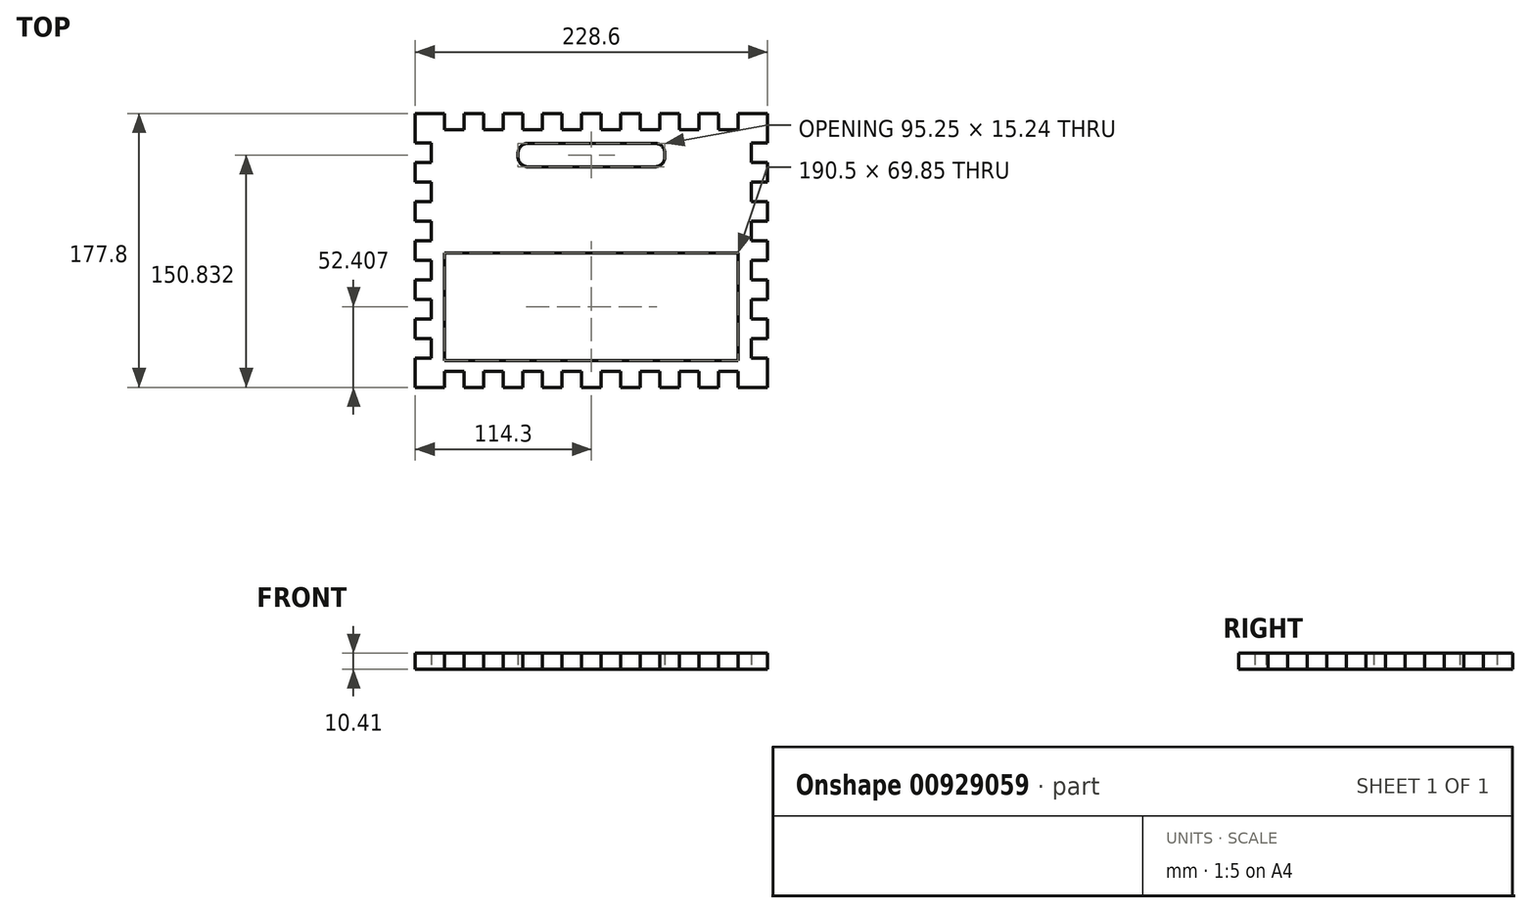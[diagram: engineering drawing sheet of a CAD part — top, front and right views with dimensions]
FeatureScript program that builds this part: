
annotation { "Feature Type Name" : "Feature", "Feature Type Description" : "" }
export const myFeature = defineFeature(function(context is Context, id is Id, definition is map)
    precondition{}
    {
        {
            var Q0;
            Q0=qCreatedBy(makeId("Top.planeOp"),FACE);
            var sketch = newSketch(context, id + "F0", { "sketchPlane" : qUnion([Q0])});
            skLineSegment(sketch, "E0.bottom", {"start": v(0, 0) * mm, "end": v(19.05, 0) * mm});
            skLineSegment(sketch, "E0.left", {"start": v(0, 0) * mm, "end": v(0, -19.05) * mm});
            skLineSegment(sketch, "E1", {"start": v(19.05, 0) * mm, "end": v(19.05, -10.41) * mm});
            skLineSegment(sketch, "E2", {"start": v(19.05, -10.41) * mm, "end": v(31.75, -10.41) * mm});
            skLineSegment(sketch, "E3", {"start": v(31.75, -10.41) * mm, "end": v(31.75, 0) * mm});
            skLineSegment(sketch, "E4", {"start": v(31.75, 0) * mm, "end": v(44.45, 0) * mm});
            skLineSegment(sketch, "E5", {"start": v(44.45, 0) * mm, "end": v(44.45, -10.41) * mm});
            skLineSegment(sketch, "E6", {"start": v(44.45, -10.41) * mm, "end": v(57.15, -10.41) * mm});
            skLineSegment(sketch, "E7", {"start": v(57.15, -10.41) * mm, "end": v(57.15, 0) * mm});
            skLineSegment(sketch, "E8", {"start": v(57.15, 0) * mm, "end": v(69.85, 0) * mm});
            skLineSegment(sketch, "E9", {"start": v(69.85, 0) * mm, "end": v(69.85, -10.41) * mm});
            skLineSegment(sketch, "E10", {"start": v(69.85, -10.41) * mm, "end": v(82.55, -10.41) * mm});
            skLineSegment(sketch, "E11", {"start": v(82.55, -10.41) * mm, "end": v(82.55, 0) * mm});
            skLineSegment(sketch, "E12.trimOffspring", {"start": v(82.55, 0) * mm, "end": v(95.25, 0) * mm});
            skLineSegment(sketch, "E13", {"start": v(95.25, 0) * mm, "end": v(95.25, -10.41) * mm});
            skLineSegment(sketch, "E14", {"start": v(95.25, -10.41) * mm, "end": v(107.95, -10.41) * mm});
            skLineSegment(sketch, "E15", {"start": v(107.95, -10.41) * mm, "end": v(107.95, 0) * mm});
            skLineSegment(sketch, "E16", {"start": v(107.95, 0) * mm, "end": v(120.65, 0) * mm});
            skLineSegment(sketch, "E17", {"start": v(120.65, 0) * mm, "end": v(120.65, -10.41) * mm});
            skLineSegment(sketch, "E18", {"start": v(120.65, -10.41) * mm, "end": v(133.35, -10.41) * mm});
            skLineSegment(sketch, "E19", {"start": v(133.35, -10.41) * mm, "end": v(133.35, 0) * mm});
            skLineSegment(sketch, "E20", {"start": v(133.35, 0) * mm, "end": v(146.05, 0) * mm});
            skLineSegment(sketch, "E21", {"start": v(146.05, 0) * mm, "end": v(146.05, -10.41) * mm});
            skLineSegment(sketch, "E22", {"start": v(146.05, -10.41) * mm, "end": v(158.75, -10.41) * mm});
            skLineSegment(sketch, "E23", {"start": v(158.75, -10.41) * mm, "end": v(158.75, 0) * mm});
            skLineSegment(sketch, "E24.trimOffspring", {"start": v(158.75, 0) * mm, "end": v(171.45, 0) * mm});
            skLineSegment(sketch, "E25", {"start": v(171.45, 0) * mm, "end": v(171.45, -10.41) * mm});
            skLineSegment(sketch, "E26", {"start": v(171.45, -10.41) * mm, "end": v(184.15, -10.41) * mm});
            skLineSegment(sketch, "E27", {"start": v(184.15, -10.41) * mm, "end": v(184.15, 0) * mm});
            skLineSegment(sketch, "E28", {"start": v(184.15, 0) * mm, "end": v(196.85, 0) * mm});
            skLineSegment(sketch, "E29", {"start": v(196.85, 0) * mm, "end": v(196.85, -10.41) * mm});
            skLineSegment(sketch, "E30", {"start": v(196.85, -10.41) * mm, "end": v(209.55, -10.41) * mm});
            skLineSegment(sketch, "E31", {"start": v(209.55, -10.41) * mm, "end": v(209.55, 0) * mm});
            skLineSegment(sketch, "E32.trimOffspring", {"start": v(209.55, 0) * mm, "end": v(228.6, 0) * mm});
            skLineSegment(sketch, "E33", {"start": v(0, -19.05) * mm, "end": v(10.41, -19.05) * mm});
            skLineSegment(sketch, "E34", {"start": v(10.41, -19.05) * mm, "end": v(10.41, -31.75) * mm});
            skLineSegment(sketch, "E35", {"start": v(10.41, -31.75) * mm, "end": v(0, -31.75) * mm});
            skLineSegment(sketch, "E36", {"start": v(0, -31.75) * mm, "end": v(0, -44.45) * mm});
            skLineSegment(sketch, "E37", {"start": v(0, -44.45) * mm, "end": v(10.41, -44.45) * mm});
            skLineSegment(sketch, "E38", {"start": v(10.41, -44.45) * mm, "end": v(10.41, -57.15) * mm});
            skLineSegment(sketch, "E39", {"start": v(10.41, -57.15) * mm, "end": v(0, -57.15) * mm});
            skLineSegment(sketch, "E40", {"start": v(0, -57.15) * mm, "end": v(0, -69.85) * mm});
            skLineSegment(sketch, "E41", {"start": v(0, -69.85) * mm, "end": v(10.41, -69.85) * mm});
            skLineSegment(sketch, "E42", {"start": v(10.41, -69.85) * mm, "end": v(10.41, -82.55) * mm});
            skLineSegment(sketch, "E43", {"start": v(10.41, -82.55) * mm, "end": v(0, -82.55) * mm});
            skLineSegment(sketch, "E44.trimOffspring", {"start": v(0, -82.55) * mm, "end": v(0, -95.25) * mm});
            skLineSegment(sketch, "E45", {"start": v(0, -95.25) * mm, "end": v(10.41, -95.25) * mm});
            skLineSegment(sketch, "E46", {"start": v(10.41, -95.25) * mm, "end": v(10.41, -107.95) * mm});
            skLineSegment(sketch, "E47", {"start": v(10.41, -107.95) * mm, "end": v(0, -107.95) * mm});
            skLineSegment(sketch, "E48", {"start": v(0, -107.95) * mm, "end": v(0, -120.65) * mm});
            skLineSegment(sketch, "E49", {"start": v(0, -120.65) * mm, "end": v(10.41, -120.65) * mm});
            skLineSegment(sketch, "E50", {"start": v(10.41, -120.65) * mm, "end": v(10.41, -133.35) * mm});
            skLineSegment(sketch, "E51", {"start": v(10.41, -133.35) * mm, "end": v(0, -133.35) * mm});
            skLineSegment(sketch, "E52", {"start": v(0, -133.35) * mm, "end": v(0, -146.05) * mm});
            skLineSegment(sketch, "E53", {"start": v(0, -146.05) * mm, "end": v(10.41, -146.05) * mm});
            skLineSegment(sketch, "E54", {"start": v(10.41, -146.05) * mm, "end": v(10.41, -158.75) * mm});
            skLineSegment(sketch, "E55", {"start": v(10.41, -158.75) * mm, "end": v(0, -158.75) * mm});
            skLineSegment(sketch, "E56.trimOffspring", {"start": v(0, -158.75) * mm, "end": v(0, -177.8) * mm});
            skLineSegment(sketch, "E57", {"start": v(114.3, 0) * mm, "end": v(114.3, 0) * mm});
            skLineSegment(sketch, "E58", {"start": v(0, -88.9) * mm, "end": v(0, -88.9) * mm});
            skLineSegment(sketch, "E59.MirrorCS", {"start": v(218.19, -82.55) * mm, "end": v(228.6, -82.55) * mm});
            skLineSegment(sketch, "E60.MirrorCS", {"start": v(228.6, -69.85) * mm, "end": v(218.19, -69.85) * mm});
            skLineSegment(sketch, "E61.MirrorCS", {"start": v(228.6, -120.65) * mm, "end": v(218.19, -120.65) * mm});
            skLineSegment(sketch, "E62.MirrorCS", {"start": v(218.19, -57.15) * mm, "end": v(228.6, -57.15) * mm});
            skLineSegment(sketch, "E63.MirrorCS", {"start": v(228.6, -95.25) * mm, "end": v(218.19, -95.25) * mm});
            skLineSegment(sketch, "E64.MirrorCS", {"start": v(218.19, -158.75) * mm, "end": v(228.6, -158.75) * mm});
            skLineSegment(sketch, "E65.MirrorCS", {"start": v(218.19, -107.95) * mm, "end": v(228.6, -107.95) * mm});
            skLineSegment(sketch, "E66.MirrorCS", {"start": v(228.6, -19.05) * mm, "end": v(218.19, -19.05) * mm});
            skLineSegment(sketch, "E67.MirrorCS", {"start": v(228.6, -44.45) * mm, "end": v(218.19, -44.45) * mm});
            skLineSegment(sketch, "E68.MirrorCS", {"start": v(218.19, -133.35) * mm, "end": v(228.6, -133.35) * mm});
            skLineSegment(sketch, "E69.MirrorCS", {"start": v(228.6, -82.55) * mm, "end": v(228.6, -95.25) * mm});
            skLineSegment(sketch, "E70.MirrorCS", {"start": v(218.19, -31.75) * mm, "end": v(228.6, -31.75) * mm});
            skLineSegment(sketch, "E71.MirrorCS", {"start": v(228.6, -146.05) * mm, "end": v(218.19, -146.05) * mm});
            skLineSegment(sketch, "E72.MirrorCS", {"start": v(228.6, 0) * mm, "end": v(228.6, -19.05) * mm});
            skLineSegment(sketch, "E73.MirrorCS", {"start": v(228.6, -133.35) * mm, "end": v(228.6, -146.05) * mm});
            skLineSegment(sketch, "E74.MirrorCS", {"start": v(228.6, -107.95) * mm, "end": v(228.6, -120.65) * mm});
            skLineSegment(sketch, "E75.MirrorCS", {"start": v(228.6, -31.75) * mm, "end": v(228.6, -44.45) * mm});
            skLineSegment(sketch, "E76.MirrorCS", {"start": v(228.6, -57.15) * mm, "end": v(228.6, -69.85) * mm});
            skLineSegment(sketch, "E77.MirrorCS", {"start": v(218.19, -19.05) * mm, "end": v(218.19, -31.75) * mm});
            skLineSegment(sketch, "E78.MirrorCS", {"start": v(218.19, -120.65) * mm, "end": v(218.19, -133.35) * mm});
            skLineSegment(sketch, "E79.MirrorCS", {"start": v(218.19, -69.85) * mm, "end": v(218.19, -82.55) * mm});
            skLineSegment(sketch, "E80.MirrorCS", {"start": v(218.19, -44.45) * mm, "end": v(218.19, -57.15) * mm});
            skLineSegment(sketch, "E81.MirrorCS", {"start": v(218.19, -146.05) * mm, "end": v(218.19, -158.75) * mm});
            skLineSegment(sketch, "E82.MirrorCS", {"start": v(218.19, -95.25) * mm, "end": v(218.19, -107.95) * mm});
            skLineSegment(sketch, "E83.MirrorCS", {"start": v(228.6, -158.75) * mm, "end": v(228.6, -177.8) * mm});
            skLineSegment(sketch, "E84.MirrorCS", {"start": v(69.85, -177.8) * mm, "end": v(69.85, -167.39) * mm});
            skLineSegment(sketch, "E85.MirrorCS", {"start": v(209.55, -167.39) * mm, "end": v(209.55, -177.8) * mm});
            skLineSegment(sketch, "E86.MirrorCS", {"start": v(19.05, -177.8) * mm, "end": v(19.05, -167.39) * mm});
            skLineSegment(sketch, "E87.MirrorCS", {"start": v(107.95, -167.39) * mm, "end": v(107.95, -177.8) * mm});
            skLineSegment(sketch, "E88.MirrorCS", {"start": v(82.55, -167.39) * mm, "end": v(82.55, -177.8) * mm});
            skLineSegment(sketch, "E89.MirrorCS", {"start": v(146.05, -177.8) * mm, "end": v(146.05, -167.39) * mm});
            skLineSegment(sketch, "E90.MirrorCS", {"start": v(44.45, -177.8) * mm, "end": v(44.45, -167.39) * mm});
            skLineSegment(sketch, "E91.MirrorCS", {"start": v(196.85, -177.8) * mm, "end": v(196.85, -167.39) * mm});
            skLineSegment(sketch, "E92.MirrorCS", {"start": v(133.35, -167.39) * mm, "end": v(133.35, -177.8) * mm});
            skLineSegment(sketch, "E93.MirrorCS", {"start": v(184.15, -167.39) * mm, "end": v(184.15, -177.8) * mm});
            skLineSegment(sketch, "E94.MirrorCS", {"start": v(158.75, -167.39) * mm, "end": v(158.75, -177.8) * mm});
            skLineSegment(sketch, "E95.MirrorCS", {"start": v(171.45, -177.8) * mm, "end": v(171.45, -167.39) * mm});
            skLineSegment(sketch, "E96.MirrorCS", {"start": v(95.25, -177.8) * mm, "end": v(95.25, -167.39) * mm});
            skLineSegment(sketch, "E97.MirrorCS", {"start": v(120.65, -177.8) * mm, "end": v(120.65, -167.39) * mm});
            skLineSegment(sketch, "E98.MirrorCS", {"start": v(57.15, -167.39) * mm, "end": v(57.15, -177.8) * mm});
            skLineSegment(sketch, "E99.MirrorCS", {"start": v(31.75, -167.39) * mm, "end": v(31.75, -177.8) * mm});
            skLineSegment(sketch, "E100.MirrorCS", {"start": v(107.95, -177.8) * mm, "end": v(120.65, -177.8) * mm});
            skLineSegment(sketch, "E101.MirrorCS", {"start": v(158.75, -177.8) * mm, "end": v(171.45, -177.8) * mm});
            skLineSegment(sketch, "E102.MirrorCS", {"start": v(82.55, -177.8) * mm, "end": v(95.25, -177.8) * mm});
            skLineSegment(sketch, "E103.MirrorCS", {"start": v(184.15, -177.8) * mm, "end": v(196.85, -177.8) * mm});
            skLineSegment(sketch, "E104.MirrorCS", {"start": v(133.35, -177.8) * mm, "end": v(146.05, -177.8) * mm});
            skLineSegment(sketch, "E105.MirrorCS", {"start": v(57.15, -177.8) * mm, "end": v(69.85, -177.8) * mm});
            skLineSegment(sketch, "E106.MirrorCS", {"start": v(31.75, -177.8) * mm, "end": v(44.45, -177.8) * mm});
            skLineSegment(sketch, "E107.MirrorCS", {"start": v(120.65, -167.39) * mm, "end": v(133.35, -167.39) * mm});
            skLineSegment(sketch, "E108.MirrorCS", {"start": v(69.85, -167.39) * mm, "end": v(82.55, -167.39) * mm});
            skLineSegment(sketch, "E109.MirrorCS", {"start": v(44.45, -167.39) * mm, "end": v(57.15, -167.39) * mm});
            skLineSegment(sketch, "E110.MirrorCS", {"start": v(146.05, -167.39) * mm, "end": v(158.75, -167.39) * mm});
            skLineSegment(sketch, "E111.MirrorCS", {"start": v(196.85, -167.39) * mm, "end": v(209.55, -167.39) * mm});
            skLineSegment(sketch, "E112.MirrorCS", {"start": v(95.25, -167.39) * mm, "end": v(107.95, -167.39) * mm});
            skLineSegment(sketch, "E113.MirrorCS", {"start": v(19.05, -167.39) * mm, "end": v(31.75, -167.39) * mm});
            skLineSegment(sketch, "E114.MirrorCS", {"start": v(171.45, -167.39) * mm, "end": v(184.15, -167.39) * mm});
            skLineSegment(sketch, "E115.MirrorCS", {"start": v(209.55, -177.8) * mm, "end": v(228.6, -177.8) * mm});
            skLineSegment(sketch, "E116.MirrorCS", {"start": v(0, -177.8) * mm, "end": v(19.05, -177.8) * mm});
            skLineSegment(sketch, "E117.bottom", {"start": v(73.02, -19.35) * mm, "end": v(155.58, -19.35) * mm});
            skLineSegment(sketch, "E117.top", {"start": v(73.02, -34.59) * mm, "end": v(155.58, -34.59) * mm});
            skLineSegment(sketch, "E117.left", {"start": v(66.67, -25.7) * mm, "end": v(66.67, -28.24) * mm});
            skLineSegment(sketch, "E117.right", {"start": v(161.93, -25.7) * mm, "end": v(161.93, -28.24) * mm});
            skLineSegment(sketch, "E118", {"start": v(114.3, 0) * mm, "end": v(114.3, -19.35) * mm, "construction": true});
            skPoint(sketch, "E119.visualSharp", {"position": v(66.68, -19.35) * mm});
            skArc(sketch, "E119.filletArc", {"start": v(73.02, -19.35) * mm, "mid": v(68.53, -21.2) * mm, "end": v(66.68, -25.7) * mm});
            skPoint(sketch, "E120.visualSharp", {"position": v(66.67, -34.59) * mm});
            skArc(sketch, "E120.filletArc", {"start": v(66.67, -28.24) * mm, "mid": v(68.53, -32.73) * mm, "end": v(73.02, -34.59) * mm});
            skPoint(sketch, "E121.visualSharp", {"position": v(161.93, -34.59) * mm});
            skArc(sketch, "E121.filletArc", {"start": v(155.58, -34.59) * mm, "mid": v(160.07, -32.73) * mm, "end": v(161.93, -28.24) * mm});
            skPoint(sketch, "E122.visualSharp", {"position": v(161.93, -19.35) * mm});
            skArc(sketch, "E122.filletArc", {"start": v(161.92, -25.7) * mm, "mid": v(160.07, -21.2) * mm, "end": v(155.58, -19.35) * mm});
            skLineSegment(sketch, "E123.bottom", {"start": v(19.05, -90.47) * mm, "end": v(209.55, -90.47) * mm});
            skLineSegment(sketch, "E123.top", {"start": v(19.05, -160.32) * mm, "end": v(209.55, -160.32) * mm});
            skLineSegment(sketch, "E123.left", {"start": v(19.05, -90.47) * mm, "end": v(19.05, -160.32) * mm});
            skLineSegment(sketch, "E123.right", {"start": v(209.55, -90.47) * mm, "end": v(209.55, -160.32) * mm});
            skSolve(sketch);
        }
        {
            var Q0;
            Q0=makeQuery(id+"F0.imprint","IMPRINT",FACE,{"disambiguationData":[TD([[makeQuery(id+"F0.imprint","IMPRINT",EDGE,{"derivedFrom":sQuery(id+"F0.wireOp",EDGE,"E0.bottom")}),-1.0]])]});
            extrude(context, id + "F1", {"entities" : qUnion([Q0]), "depth" : 10.4 * mm, "offsetDistance" : 25.4 * mm});
        }
    });
